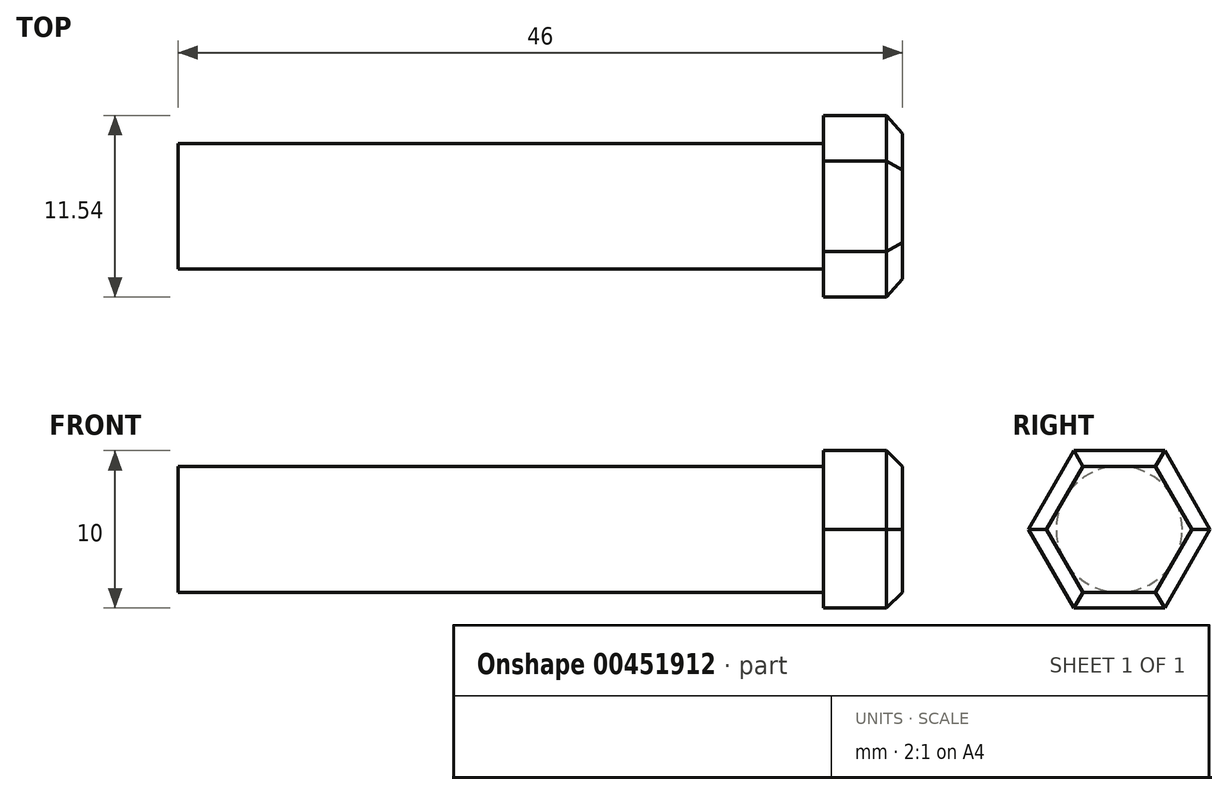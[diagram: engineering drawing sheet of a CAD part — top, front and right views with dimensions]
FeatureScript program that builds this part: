
annotation { "Feature Type Name" : "Feature", "Feature Type Description" : "" }
export const myFeature = defineFeature(function(context is Context, id is Id, definition is map)
    precondition{}
    {
        {
            var Q0;
            Q0=qCreatedBy(makeId("Right.planeOp"),FACE);
            var sketch = newSketch(context, id + "F0", { "sketchPlane" : qUnion([Q0])});
            skCircle(sketch, "E0", {"center": v(0, 0) * mm, "radius": 4 * mm});
            skSolve(sketch);
        }
        {
            var Q0;
            Q0=qSketchRegion(id+"F0",true);
            extrude(context, id + "F1", {"entities" : qUnion([Q0]), "endBound" : BoundingType.SYMMETRIC, "depth" : 41 * mm});
        }
        {
            var Q0;
            Q0=makeQuery(id+"F1.opExtrude","CAP_FACE",FACE,{"disambiguationData":[OSD([sQuery(id+"F0.wireOp",EDGE,"E0")])],"isStart":false});
            var sketch = newSketch(context, id + "F2", { "sketchPlane" : qUnion([Q0])});
            skCircle(sketch, "E1.cCircle", {"center": v(0, 0) * mm, "radius": 5 * mm, "construction": true});
            skLineSegment(sketch, "E1.0", {"start": v(-2.89, 5) * mm, "end": v(2.89, 5) * mm});
            skLineSegment(sketch, "E1.1", {"start": v(2.89, 5) * mm, "end": v(5.77, 0) * mm});
            skLineSegment(sketch, "E1.2", {"start": v(5.77, 0) * mm, "end": v(2.89, -5) * mm});
            skLineSegment(sketch, "E1.3", {"start": v(2.89, -5) * mm, "end": v(-2.89, -5) * mm});
            skLineSegment(sketch, "E1.4", {"start": v(-2.89, -5) * mm, "end": v(-5.77, 0) * mm});
            skLineSegment(sketch, "E1.5", {"start": v(-5.77, 0) * mm, "end": v(-2.89, 5) * mm});
            skPoint(sketch, "E1.0.midPoint", {"position": v(0, 5) * mm});
            skSolve(sketch);
        }
        {
            var Q0;
            Q0=qSketchRegion(id+"F2",true);
            extrude(context, id + "F3", {"entities" : qUnion([Q0]), "operationType" : NewBodyOperationType.ADD, "depth" : 5 * mm});
        }
        {
            var Q0;
            Q0=makeQuery(id+"F3.opExtrude","CAP_FACE",FACE,{"disambiguationData":[OSD([sQuery(id+"F2.wireOp",EDGE,"E1.0"),sQuery(id+"F2.wireOp",EDGE,"E1.1"),sQuery(id+"F2.wireOp",EDGE,"E1.2"),sQuery(id+"F2.wireOp",EDGE,"E1.3"),sQuery(id+"F2.wireOp",EDGE,"E1.4"),sQuery(id+"F2.wireOp",EDGE,"E1.5")])],"isStart":false});
            chamfer(context, id + "F4", {"entities" : qUnion([Q0]), "width" : 1 * mm, "tangentPropagation" : true});
        }
    });
